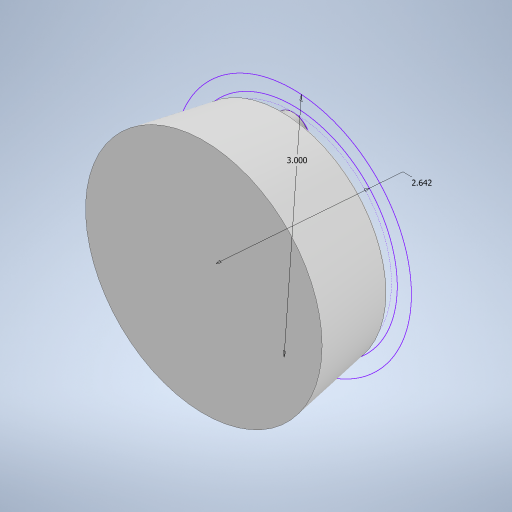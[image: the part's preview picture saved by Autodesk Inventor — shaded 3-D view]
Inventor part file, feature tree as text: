
AUTODESK INVENTOR PART (.ipt)
format: ipt  version: 2024 (Build 280153000, 153)  size: 779,264 bytes
history: native  units: in
note: dims shown in document units (in); Inventor stores cm internally (conversion verified against a paired STEP export)
features: fillet x4, sketch x2, extrude x2
ambient origin geometry x8: Origin, YZ Plane, XZ Plane, XY Plane, X Axis, Y Axis, Z Axis, Center Point
bodies: Body1 (feature_tree)
feature tree (8):
  sketch  "Sketch4"  dims[d4=0.125in d5=0.0618in d14=2.6417in]
  extrude  "Extrusion3"  Depth=2.6417in
  extrude  "Extrusion6"  Depth=0.005in
  fillet  "Fillet1"  Radius=1.0in
  fillet  "Fillet2"  Radius=0.025in
  fillet  "Fillet3"  Radius=0.005in
  fillet  "Fillet4"  Radius=0.005in
  sketch  "Sketch6"  dims[d15=3.0in d16=2.6417in d17=1.0in d18=0.0687in d19=0.025in d20=0.005in d21=0.005in d22=0.005in d23=0.0344in]
